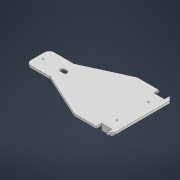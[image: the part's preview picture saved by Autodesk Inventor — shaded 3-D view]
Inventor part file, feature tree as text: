
AUTODESK INVENTOR PART (.ipt)
format: ipt  version: 2022 (Build 260153000, 153)  size: 195,584 bytes
history: native  units: in
note: dims shown in document units (in); Inventor stores cm internally (conversion verified against a paired STEP export)
features: sketch x11, extrude x8, fillet x2, chamfer x2, hole x1
ambient origin geometry x8: Origin, YZ Plane, XZ Plane, XY Plane, X Axis, Y Axis, Z Axis, Center Point
bodies: Solid1 (feature_tree)
feature tree (24):
  extrude  "Extrusion1"  Depth=0.7874in
  fillet  "Fillet1"  Radius=3.937in
  fillet  "Fillet2"  Radius=0.7874in
  chamfer  "Chamfer1"  Distance=1.5748in Angle=45.0deg
  chamfer  "Chamfer2"  Distance=1.5748in Angle=45.0deg
  sketch  "Sketch3"  dims[d19=1.9685in]
  sketch  "Sketch4"  dims[d20=1.9685in d21=1.5748in d22=0.0787in d23=45.0deg d24=1.5748in d25=0.0787in d26=45.0deg]
  extrude  "Extrusion2"  Depth=1.378in
  hole  "Hole1"  [1 undecoded]
  extrude  "Extrusion3"  Depth=3.937in
  extrude  "Extrusion4"  Depth=0.3937in
  extrude  "Extrusion5"  Depth=3.937in
  extrude  "Extrusion6"  Depth=2.3622in TaperAngle=0.0deg
  extrude  "Extrusion7"  Depth=0.7874in TaperAngle=0.0deg
  extrude  "Extrusion8"  Depth=0.0394in TaperAngle=0.0deg
  sketch  "Sketch1"  dims[d12=11.811in d13=13.7795in d16=3.937in d17=0.7874in d18=0.0in]
  sketch  "Sketch5"  dims[d27=2.3622in d28=1.378in]
  sketch  "Sketch6"  dims[d30=0.7874in d31=0.0in d33=1.9685in]
  sketch  "Sketch7"  dims[d34=0.3937in d35=0.2362in d36=0.1575in d37=0.0787in d38=90.0deg d39=0.315in d40=0.8108in d41=3.937in]
  sketch  "Sketch8"  dims[d42=1.5748in d43=0.0in d45=0.3937in]
  sketch  "Sketch9"  dims[d46=2.3622in d47=0.0in d48=3.937in]
  sketch  "Sketch10"  dims[d49=1.9685in d50=2.3622in d51=0.0in]
  sketch  "Sketch11"  dims[d53=7.874in d54=0.7874in d55=0.0in]
  sketch  "Sketch12"  dims[d56=0.0394in d57=0.0in d58=0.0394in d59=0.0in d29=0.0197in d32=0.0344in d44=0.0295in d52=0.0197in]
note: 1 required parameter value undecoded (feature->parameter linkage not recoverable at this tier; creation-order binding heuristic only, values carry confidence <= 0.55)
